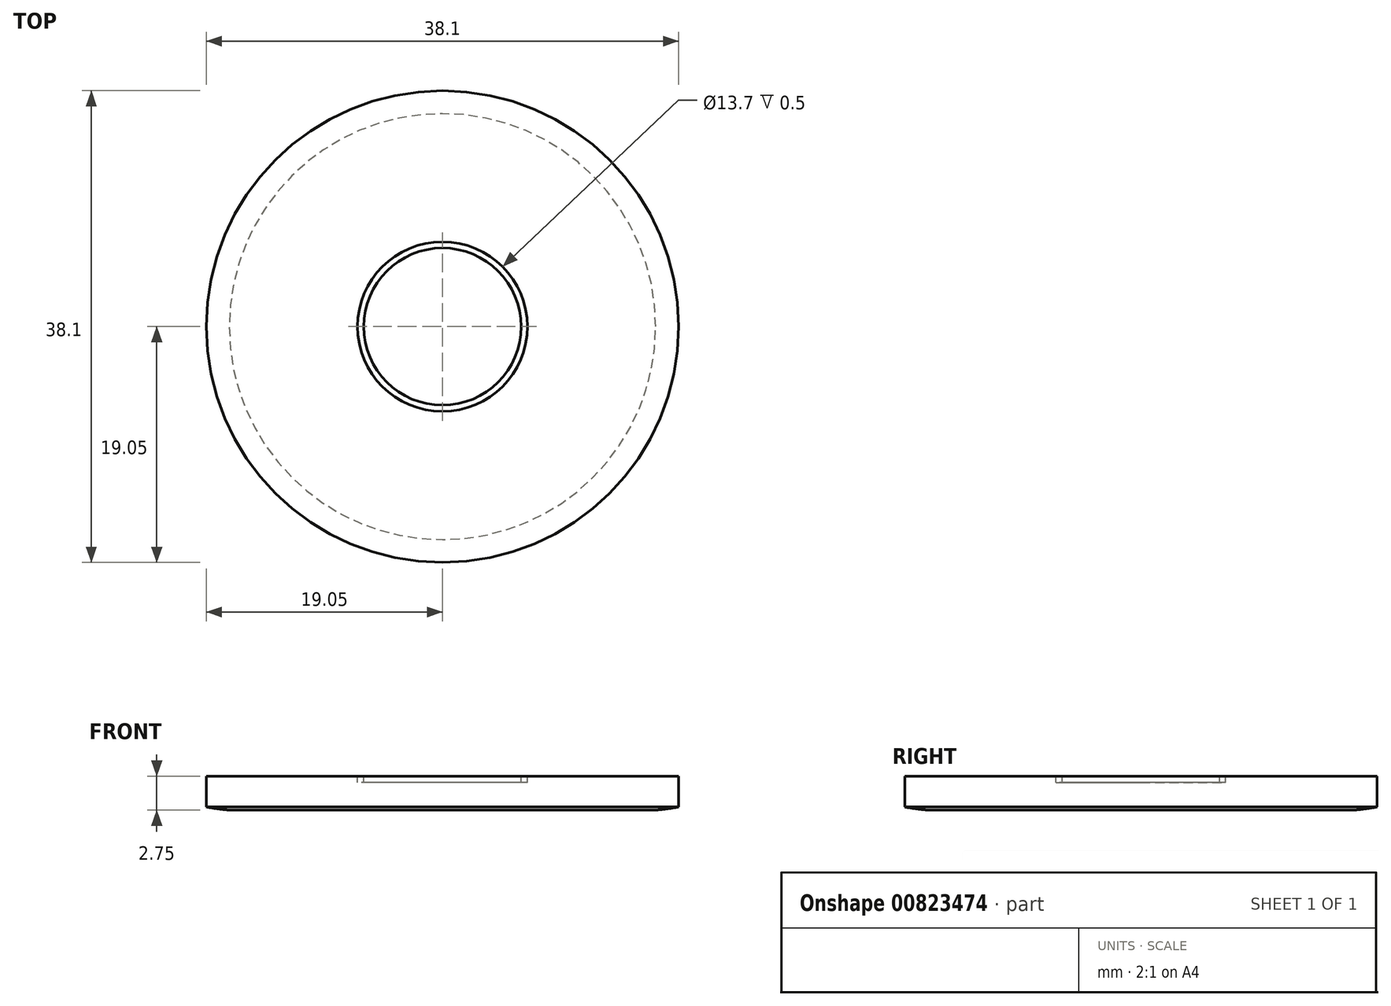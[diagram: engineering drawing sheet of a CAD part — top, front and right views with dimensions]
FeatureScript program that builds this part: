
annotation { "Feature Type Name" : "Feature", "Feature Type Description" : "" }
export const myFeature = defineFeature(function(context is Context, id is Id, definition is map)
    precondition{}
    {
        {
            var Q0;
            Q0=qCreatedBy(makeId("Top.planeOp"),FACE);
            var sketch = newSketch(context, id + "F0", { "sketchPlane" : qUnion([Q0])});
            skCircle(sketch, "E0", {"center": v(0, 0) * mm, "radius": 19.05 * mm});
            skSolve(sketch);
        }
        {
            var Q0;
            Q0=makeQuery(id+"F0.imprint","IMPRINT",FACE,{"disambiguationData":[TD([[makeQuery(id+"F0.imprint","IMPRINT",EDGE,{"derivedFrom":sQuery(id+"F0.wireOp",EDGE,"E0")}),1.0]])]});
            extrude(context, id + "F1", {"entities" : qUnion([Q0]), "depth" : 2.5 * mm, "offsetDistance" : 25 * mm});
        }
        {
            var Q0;
            Q0=makeQuery(id+"F1.opExtrude","CAP_FACE",FACE,{"disambiguationData":[OSD([sQuery(id+"F0.wireOp",EDGE,"E0")])],"isStart":false});
            var sketch = newSketch(context, id + "F2", { "sketchPlane" : qUnion([Q0])});
            skCircle(sketch, "E1", {"center": v(0, 0) * mm, "radius": 6.35 * mm});
            skCircle(sketch, "E2", {"center": v(0, 0) * mm, "radius": 6.85 * mm});
            skSolve(sketch);
        }
        {
            var Q0;
            Q0=makeQuery(id+"F2.imprint","IMPRINT",FACE,{"disambiguationData":[TD([[makeQuery(id+"F2.imprint","IMPRINT",EDGE,{"derivedFrom":sQuery(id+"F2.wireOp",EDGE,"E1")}),-1.0]])]});
            extrude(context, id + "F3", {"entities" : qUnion([Q0]), "operationType" : NewBodyOperationType.REMOVE, "oppositeDirection" : true, "depth" : .5 * mm, "offsetDistance" : 25 * mm});
        }
        {
            var Q0;
            Q0=qCreatedBy(makeId("Front.planeOp"),FACE);
            var sketch = newSketch(context, id + "F4", { "sketchPlane" : qUnion([Q0])});
            skLineSegment(sketch, "E3.0", {"start": v(-19.05, 0) * mm, "end": v(0, 0) * mm});
            skLineSegment(sketch, "E4", {"start": v(0, 0) * mm, "end": v(0, -0.25) * mm});
            skArc(sketch, "E5", {"start": v(-19.05, 0) * mm, "mid": v(-18.12, -0.14) * mm, "end": v(-17.2, -0.25) * mm});
            skLineSegment(sketch, "E6", {"start": v(0, -0.25) * mm, "end": v(-17.2, -0.25) * mm});
            skPoint(sketch, "E7.trimOffspring.start.orphan", {"position": v(0, -0.5) * mm});
            skPoint(sketch, "E8.orphan", {"position": v(19.05, 0) * mm});
            skSolve(sketch);
        }
        {
            var Q0;
            Q0=makeQuery(id+"F4.imprint","IMPRINT",FACE,{"disambiguationData":[TD([[makeQuery(id+"F4.imprint","IMPRINT",EDGE,{"derivedFrom":sQuery(id+"F4.wireOp",EDGE,"E3.0")}),-1.0]])]});
            var Q1;
            Q1=sQuery(id+"F4.wireOp",EDGE,"E4");
            revolve(context, id + "F5", {"surfaceOperationType" : NewSurfaceOperationType.NEW, "entities" : qUnion([Q0]), "axis" : qUnion([Q1]), "revolveType" : RevolveType.FULL});
        }
    });
